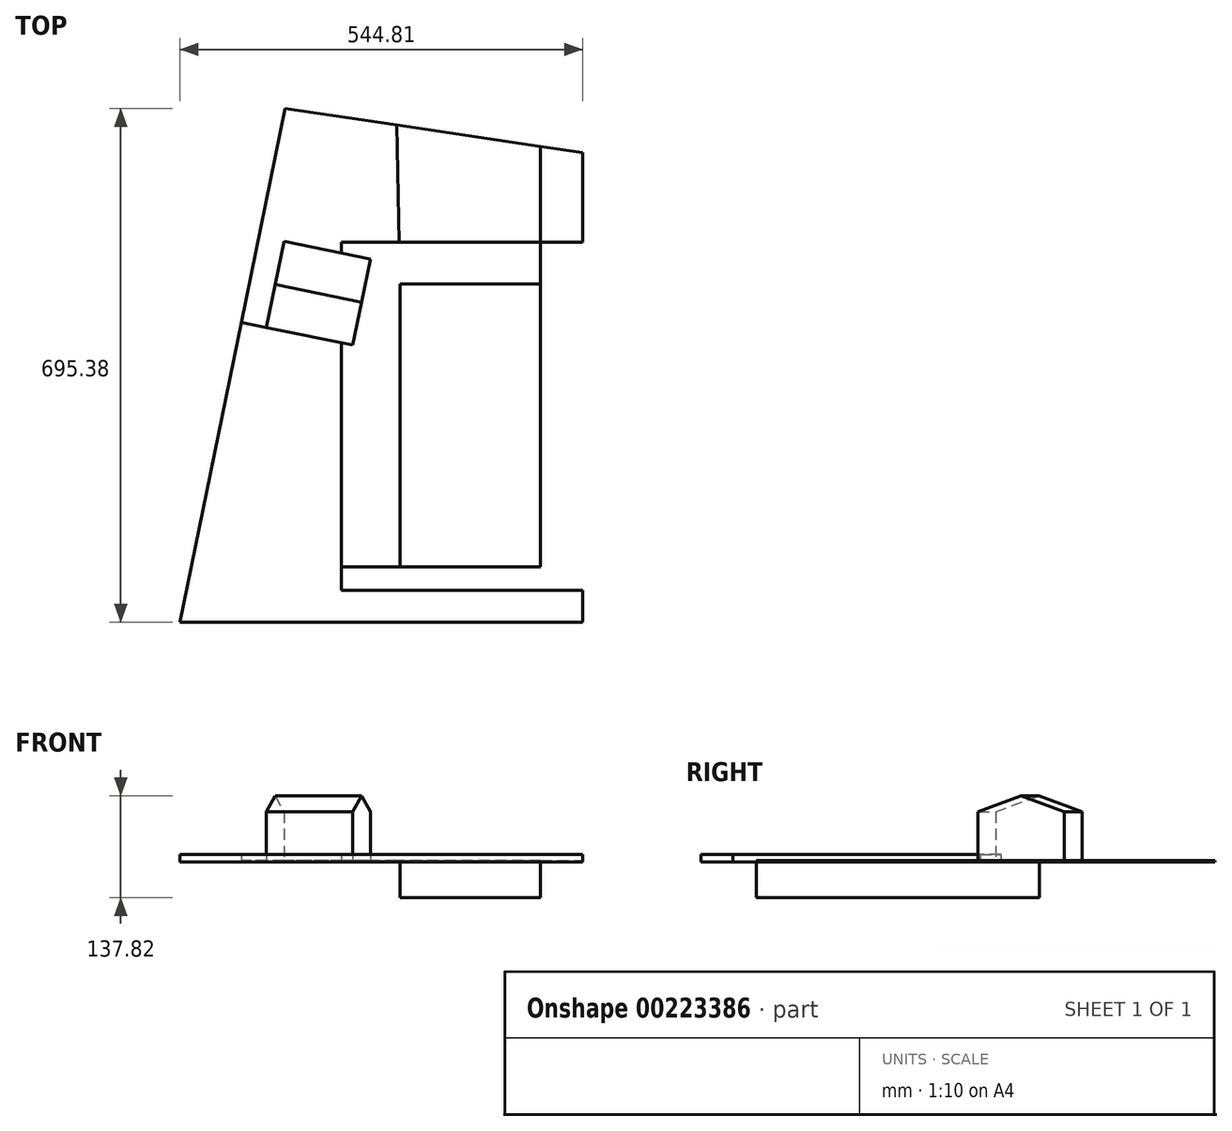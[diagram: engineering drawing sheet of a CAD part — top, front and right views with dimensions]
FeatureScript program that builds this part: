
annotation { "Feature Type Name" : "Feature", "Feature Type Description" : "" }
export const myFeature = defineFeature(function(context is Context, id is Id, definition is map)
    precondition{}
    {
        {
            var Q0;
            Q0=qCreatedBy(makeId("Top.planeOp"),FACE);
            var sketch = newSketch(context, id + "F0", { "sketchPlane" : qUnion([Q0])});
            skLineSegment(sketch, "E0", {"start": v(-196.34, 336.38) * mm, "end": v(-323.41, -284) * mm});
            skLineSegment(sketch, "E1", {"start": v(-323.41, -284) * mm, "end": v(149.04, -284) * mm});
            skLineSegment(sketch, "E2", {"start": v(149.04, -284) * mm, "end": v(149.04, 285) * mm, "construction": true});
            skLineSegment(sketch, "E3", {"start": v(149.04, 285) * mm, "end": v(-196.34, 336.38) * mm});
            skLineSegment(sketch, "E4", {"start": v(-244.96, 99) * mm, "end": v(149.04, 99) * mm, "construction": true});
            skLineSegment(sketch, "E5", {"start": v(-40.96, 99) * mm, "end": v(-45.57, 313.95) * mm, "construction": true});
            skLineSegment(sketch, "E6", {"start": v(149.04, 99) * mm, "end": v(149.04, -284) * mm});
            skLineSegment(sketch, "E7.bottom", {"start": v(-40.96, 99) * mm, "end": v(149.04, 99) * mm});
            skLineSegment(sketch, "E7.top", {"start": v(-40.96, -284) * mm, "end": v(149.04, -284) * mm});
            skLineSegment(sketch, "E7.left", {"start": v(-40.96, 99) * mm, "end": v(-40.96, -284) * mm});
            skLineSegment(sketch, "E8", {"start": v(-323.41, -284) * mm, "end": v(-338.77, -359) * mm});
            skLineSegment(sketch, "E9", {"start": v(-338.77, -359) * mm, "end": v(149.04, -359) * mm});
            skLineSegment(sketch, "E10", {"start": v(149.04, -359) * mm, "end": v(149.04, -284) * mm});
            skPoint(sketch, "E11", {"position": v(-40.96, 16) * mm});
            skLineSegment(sketch, "E12", {"start": v(-40.96, 16) * mm, "end": v(-261.96, 16) * mm, "construction": true});
            skLineSegment(sketch, "E13", {"start": v(149.04, 285) * mm, "end": v(206.04, 276.52) * mm});
            skLineSegment(sketch, "E14", {"start": v(206.04, 276.52) * mm, "end": v(206.04, -359) * mm});
            skLineSegment(sketch, "E15", {"start": v(206.04, -359) * mm, "end": v(149.04, -359) * mm});
            skLineSegment(sketch, "E16", {"start": v(206.04, 155) * mm, "end": v(-233.5, 155) * mm, "construction": true});
            skLineSegment(sketch, "E17", {"start": v(206.04, -316) * mm, "end": v(-119.96, -316) * mm});
            skLineSegment(sketch, "E18", {"start": v(-119.96, -316) * mm, "end": v(-119.96, 155) * mm});
            skLineSegment(sketch, "E19", {"start": v(-119.96, 155) * mm, "end": v(206.04, 155) * mm});
            skLineSegment(sketch, "E20", {"start": v(-197.82, 156.45) * mm, "end": v(-221.7, 39.87) * mm});
            skLineSegment(sketch, "E21", {"start": v(-221.7, 39.87) * mm, "end": v(-105.12, 16) * mm});
            skLineSegment(sketch, "E22", {"start": v(-105.12, 16) * mm, "end": v(-81.24, 132.58) * mm});
            skLineSegment(sketch, "E23", {"start": v(-81.24, 132.58) * mm, "end": v(-197.82, 156.45) * mm});
            skLineSegment(sketch, "E24", {"start": v(-221.7, 39.87) * mm, "end": v(-255.65, 46.83) * mm});
            skLineSegment(sketch, "E25", {"start": v(-40.96, 99) * mm, "end": v(-45.57, 313.95) * mm});
            skLineSegment(sketch, "E26", {"start": v(149.04, 99) * mm, "end": v(149.04, 285) * mm});
            skSolve(sketch);
        }
        {
            var Q0;
            Q0=makeQuery(id+"F0.imprint","IMPRINT",FACE,{"disambiguationData":[TD([[makeQuery(id+"F0.imprint","IMPRINT",EDGE,{"derivedFrom":sQuery(id+"F0.wireOp",EDGE,"E7.bottom")}),-1.0]])]});
            extrude(context, id + "F1", {"entities" : qUnion([Q0]), "oppositeDirection" : true, "offsetDistance" : 25 * mm, "depth" : 48 * mm});
        }
        {
            var Q0;
            Q0=makeQuery(id+"F0.imprint","IMPRINT",FACE,{"disambiguationData":[TD([[makeQuery(id+"F0.imprint","IMPRINT",EDGE,{"derivedFrom":sQuery(id+"F0.wireOp",EDGE,"E7.bottom")}),1.0]])]});
            var Q1;
            {var subQ1=sQuery(id+"F0.wireOp",EDGE,"E7.top");Q1=makeQuery(id+"F0.imprint","IMPRINT",FACE,{"disambiguationData":[TD([[makeQuery(id+"F0.imprint","IMPRINT",EDGE,{"derivedFrom":subQ1}),-1.0]])]});}
            var Q2;
            {var subQ6=sQuery(id+"F0.wireOp",EDGE,"E7.left");Q2=makeQuery(id+"F0.imprint","IMPRINT",FACE,{"disambiguationData":[TD([[makeQuery(id+"F0.imprint","IMPRINT",EDGE,{"derivedFrom":subQ6}),-1.0]])]});}
            var Q3;
            {var subQ8=sQuery(id+"F0.wireOp",EDGE,"E6");Q3=makeQuery(id+"F0.imprint","IMPRINT",FACE,{"disambiguationData":[TD([[makeQuery(id+"F0.imprint","IMPRINT",EDGE,{"derivedFrom":subQ8}),1.0]])]});}
            extrude(context, id + "F2", {"entities" : qUnion([Q0, Q1, Q2, Q3]), "offsetDistance" : 25 * mm, "depth" : 2 * mm});
        }
        {
            var Q0;
            {var subQ0=sQuery(id+"F0.wireOp",EDGE,"E24");Q0=makeQuery(id+"F0.imprint","IMPRINT",FACE,{"disambiguationData":[TD([[makeQuery(id+"F0.imprint","IMPRINT",EDGE,{"derivedFrom":subQ0}),1.0]])]});}
            var Q1;
            {var subQ4=sQuery(id+"F0.wireOp",EDGE,"E8");Q1=makeQuery(id+"F0.imprint","IMPRINT",FACE,{"disambiguationData":[TD([[makeQuery(id+"F0.imprint","IMPRINT",EDGE,{"derivedFrom":subQ4}),1.0]])]});}
            var Q2;
            {var subQ0=sQuery(id+"F0.wireOp",EDGE,"E15");Q2=makeQuery(id+"F0.imprint","IMPRINT",FACE,{"disambiguationData":[TD([[makeQuery(id+"F0.imprint","IMPRINT",EDGE,{"derivedFrom":subQ0}),-1.0]])]});}
            extrude(context, id + "F3", {"entities" : qUnion([Q0, Q1, Q2]), "offsetDistance" : 25 * mm, "depth" : 10.5 * mm});
        }
        {
            var Q0;
            {var subQ5=sQuery(id+"F0.wireOp",EDGE,"E20");Q0=makeQuery(id+"F0.imprint","IMPRINT",FACE,{"disambiguationData":[TD([[makeQuery(id+"F0.imprint","IMPRINT",EDGE,{"derivedFrom":subQ5}),1.0]])]});}
            var Q1;
            {var subQ5=sQuery(id+"F0.wireOp",EDGE,"E22");Q1=makeQuery(id+"F0.imprint","IMPRINT",FACE,{"disambiguationData":[TD([[makeQuery(id+"F0.imprint","IMPRINT",EDGE,{"derivedFrom":subQ5}),1.0]])]});}
            extrude(context, id + "F4", {"entities" : qUnion([Q0, Q1]), "offsetDistance" : 25 * mm, "depth" : 90 * mm});
        }
        {
            var Q0;
            {var subQ5=sQuery(id+"F0.wireOp",EDGE,"E3");Q0=makeQuery(id+"F0.imprint","IMPRINT",FACE,{"disambiguationData":[TD([[makeQuery(id+"F0.imprint","IMPRINT",EDGE,{"derivedFrom":subQ5}),1.0]])]});}
            extrude(context, id + "F5", {"entities" : qUnion([Q0]), "offsetDistance" : 25 * mm, "depth" : 2 * mm});
        }
        {
            var Q0;
            Q0=makeQuery(id+"F4.opExtrude","CAP_EDGE",EDGE,{"disambiguationData":[OSD([sQuery(id+"F0.wireOp",EDGE,"E21")])],"isStart":false});
            var Q1;
            Q1=makeQuery(id+"F4.opExtrude","CAP_EDGE",EDGE,{"disambiguationData":[OSD([sQuery(id+"F0.wireOp",EDGE,"E23")])],"isStart":false});
            chamfer(context, id + "F6", {"entities" : qUnion([Q0, Q1]), "chamferType" : ChamferType.OFFSET_ANGLE, "width" : 60 * mm, "oppositeDirection" : false, "angle" : 20 * degree, "tangentPropagation" : true});
        }
        {
            var Q0;
            {var subQ12=sQuery(id+"F0.wireOp",EDGE,"E20");Q0=makeQuery(id+"F0.imprint","IMPRINT",FACE,{"disambiguationData":[TD([[makeQuery(id+"F0.imprint","IMPRINT",EDGE,{"derivedFrom":subQ12}),-1.0]])]});}
            var Q1;
            {var subQ0=sQuery(id+"F0.wireOp",EDGE,"E13");Q1=makeQuery(id+"F0.imprint","IMPRINT",FACE,{"disambiguationData":[TD([[makeQuery(id+"F0.imprint","IMPRINT",EDGE,{"derivedFrom":subQ0}),-1.0]])]});}
            var Q2;
            Q2=makeQuery(id+"F5.opExtrude","CAP_FACE",FACE,{"disambiguationData":[OSD([sQuery(id+"F0.wireOp",EDGE,"E3"),sQuery(id+"F0.wireOp",EDGE,"E19"),sQuery(id+"F0.wireOp",EDGE,"E25"),sQuery(id+"F0.wireOp",EDGE,"E26")])],"isStart":false});
            extrude(context, id + "F7", {"entities" : qUnion([Q0, Q1]), "endBound" : BoundingType.UP_TO_SURFACE, "depth" : 25 * mm, "endBoundEntityFace" : qUnion([Q2]), "offsetDistance" : 25 * mm});
        }
    });
